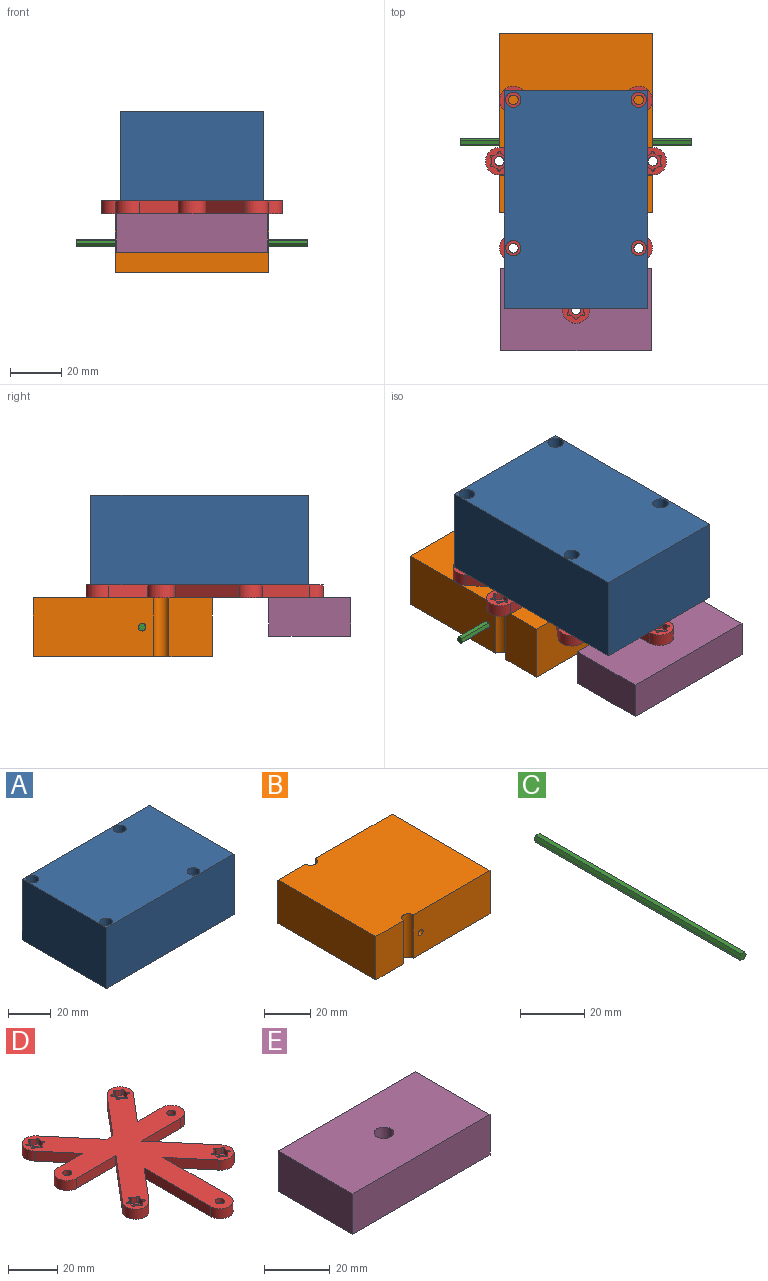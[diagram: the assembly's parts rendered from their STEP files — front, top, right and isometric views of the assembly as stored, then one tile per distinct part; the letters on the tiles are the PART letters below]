
ASSEMBLY  parts=5 mates=4
PART A: 10 faces, bbox 85x56x35 mm
  f0: plane 85x35mm, normal (0,1,0), area 2975mm2, adj f1,f3,f4,f5
  f1: plane 56x35mm, normal (-1,0,0), area 1960mm2, adj f0,f2,f4,f5
  f2: plane 85x35mm, normal (0,-1,0), area 2975mm2, adj f1,f3,f4,f5
  f3: plane 56x35mm, normal (1,0,0), area 1960mm2, adj f0,f2,f4,f5
  f4: plane 85x56mm, normal (0,0,1), area 4646.9mm2, adj f0,f1,f2,f3,f6,f7,f8,f9
  f5: plane 85x56mm, normal (0,0,-1), area 4646.9mm2, adj f0,f1,f2,f3,f6,f7,f8,f9
  f6: cylinder r=3mm len=35mm, axis (0,0,-1), area 659.7mm2, adj f4,f5
  f7: cylinder r=3mm len=35mm, axis (0,0,-1), area 659.7mm2, adj f4,f5
  f8: cylinder r=3mm len=35mm, axis (0,0,-1), area 659.7mm2, adj f4,f5
  f9: cylinder r=3mm len=35mm, axis (0,0,-1), area 659.7mm2, adj f4,f5
PART B: 11 faces, bbox 70x60x23 mm
  f0: plane 47x23mm, normal (0,1,0), area 1073.9mm2, adj f4,f6,f7,f9,f10
  f1: plane 23x17mm, normal (0,1,0), area 391mm2, adj f4,f5,f7,f9
  f2: plane 47x23mm, normal (0,-1,0), area 1073.9mm2, adj f4,f6,f7,f8,f10
  f3: plane 23x17mm, normal (0,-1,0), area 391mm2, adj f4,f5,f7,f8
  f4: plane 70x60mm, normal (0,0,1), area 4171.7mm2, adj f0,f1,f2,f3,f5,f6,f8,f9
  f5: plane 60x23mm, normal (-1,0,0), area 1380mm2, adj f1,f3,f4,f7
  f6: plane 60x23mm, normal (1,0,0), area 1380mm2, adj f0,f2,f4,f7
  f7: plane 70x60mm, normal (0,0,-1), area 4171.7mm2, adj f0,f1,f2,f3,f5,f6,f8,f9
  f8: cylinder r=3mm len=23mm, axis (0,0,-1), area 216.8mm2, adj f2,f3,f4,f7
  f9: cylinder r=3mm len=23mm, axis (0,0,-1), area 216.8mm2, adj f0,f1,f4,f7
  f10: cylinder r=1.5mm len=60mm, axis (0,1,0), area 565.5mm2, adj f0,f2
PART C: 8 faces, bbox 3x90x2.6 mm
  f0: plane 90x1.5mm, normal (0,0,-1), area 135mm2, adj f1,f5,f6,f7
  f1: plane 90x1.3mm, normal (0.87,0,-0.5), area 135mm2, adj f0,f2,f6,f7
  f2: plane 90x1.3mm, normal (0.87,0,0.5), area 135mm2, adj f1,f3,f6,f7
  f3: plane 90x1.5mm, normal (0,0,1), area 135mm2, adj f2,f4,f6,f7
  f4: plane 90x1.3mm, normal (-0.87,0,0.5), area 135mm2, adj f3,f5,f6,f7
  f5: plane 90x1.3mm, normal (-0.87,0,-0.5), area 135mm2, adj f0,f4,f6,f7
  f6: plane 3x2.6mm, normal (0,-1,0), area 5.8mm2, adj f0,f1,f2,f3,f4,f5
  f7: plane 3x2.6mm, normal (0,1,0), area 5.8mm2, adj f0,f1,f2,f3,f4,f5
PART D: 122 faces, bbox 70.8x92.8x5 mm
  f0: cylinder r=5.38mm len=10.75mm, axis (0,0,-1), area 84.4mm2, adj f1,f21,f22,f23
  f1: plane 22.65x5mm, normal (0,-1,0), area 113.2mm2, adj f0,f2,f22,f23
  f2: plane 25.16x21.25mm, normal (-0.76,0.65,0), area 164.7mm2, adj f1,f3,f22,f23
  f3: cylinder r=5.38mm len=9.48mm, axis (0,0,-1), area 84.4mm2, adj f2,f4,f22,f23
  f4: plane 17.78x15.02mm, normal (0.76,-0.65,0), area 116.4mm2, adj f3,f5,f22,f23
  f5: plane 38.31x5mm, normal (-1,0,0), area 191.5mm2, adj f4,f6,f22,f23
  f6: cylinder r=5.38mm len=10.75mm, axis (0,0,-1), area 84.4mm2, adj f5,f7,f22,f23
  f7: plane 38.31x5mm, normal (1,0,0), area 191.5mm2, adj f6,f8,f22,f23
  f8: plane 17.78x15.02mm, normal (-0.76,-0.65,0), area 116.4mm2, adj f7,f9,f22,f23
  f9: cylinder r=5.38mm len=9.48mm, axis (0,0,-1), area 84.4mm2, adj f8,f10,f22,f23
  f10: plane 25.16x21.25mm, normal (0.76,0.65,0), area 164.7mm2, adj f9,f11,f22,f23
  f11: plane 22.65x5mm, normal (0,-1,0), area 113.2mm2, adj f10,f12,f22,f23
  f12: cylinder r=5.38mm len=10.75mm, axis (0,0,-1), area 84.4mm2, adj f11,f13,f22,f23
  f13: plane 14.2x5mm, normal (0,1,0), area 71mm2, adj f12,f14,f22,f23
  f14: plane 15.16x12.8mm, normal (0.76,-0.65,0), area 99.2mm2, adj f13,f15,f22,f23
  f15: cylinder r=5.38mm len=9.48mm, axis (0,0,-1), area 84.4mm2, adj f14,f16,f22,f23
  f16: plane 22.09x18.67mm, normal (-0.76,0.65,0), area 144.6mm2, adj f15,f17,f22,f23
  f17: plane 5x3.46mm, normal (0,1,0), area 17.3mm2, adj f16,f18,f22,f23
  f18: plane 22.09x18.67mm, normal (0.76,0.65,0), area 144.6mm2, adj f17,f19,f22,f23
  f19: cylinder r=5.38mm len=9.48mm, axis (0,0,-1), area 84.4mm2, adj f18,f20,f22,f23
  f20: plane 15.16x12.8mm, normal (-0.76,-0.65,0), area 99.2mm2, adj f19,f21,f22,f23
  f21: plane 14.2x5mm, normal (0,1,0), area 71mm2, adj f0,f20,f22,f23
  f22: plane 92.75x70.75mm, normal (0,0,1), area 2521mm2, adj f0,f1,f2,f3,f4,f5,f6,f7
  f23: plane 92.75x70.75mm, normal (0,0,-1), area 2542.7mm2, adj f0,f1,f2,f3,f4,f5,f6,f7
  f24: plane 2.8x2.06mm, normal (-0.5,-0.87,0), area 6.6mm2, adj f23,f31,f35,f36
  f25: plane 2.8x2.38mm, normal (1,0,0), area 6.7mm2, adj f23,f30,f34,f36
  f26: plane 2.8x2.38mm, normal (-1,0,0), area 6.7mm2, adj f23,f32,f35,f36
  f27: plane 2.8x2.06mm, normal (0.5,0.87,0), area 6.6mm2, adj f23,f33,f34,f36
  f28: plane 2.8x2.06mm, normal (-0.5,0.87,0), area 6.6mm2, adj f23,f32,f33,f36
  f29: plane 2.8x2.06mm, normal (0.5,-0.87,0), area 6.6mm2, adj f23,f30,f31,f36
  f30: cylinder r=0.5mm len=2.8mm, axis (0,0,-1), area 5.9mm2, adj f23,f25,f29,f36
  f31: cylinder r=0.5mm len=2.8mm, axis (0,0,-1), area 5.9mm2, adj f23,f24,f29,f36
  f32: cylinder r=0.5mm len=2.8mm, axis (0,0,-1), area 5.9mm2, adj f23,f26,f28,f36
  f33: cylinder r=0.5mm len=2.8mm, axis (0,0,-1), area 5.9mm2, adj f23,f27,f28,f36
  f34: cylinder r=0.5mm len=2.8mm, axis (0,0,-1), area 5.9mm2, adj f23,f25,f27,f36
  f35: cylinder r=0.5mm len=2.8mm, axis (0,0,-1), area 5.9mm2, adj f23,f24,f26,f36
  f36: plane 7.75x6.85mm, normal (0,0,-1), area 21.7mm2, adj f24,f25,f26,f27,f28,f29,f30,f31
  f37: cylinder r=1.88mm len=3.75mm, axis (0,0,-1), area 25.9mm2, adj f22,f36
  f38: plane 2.8x2.06mm, normal (-0.5,-0.87,0), area 6.6mm2, adj f23,f45,f49,f50
  f39: plane 2.8x2.38mm, normal (1,0,0), area 6.7mm2, adj f23,f44,f48,f50
  f40: plane 2.8x2.38mm, normal (-1,0,0), area 6.7mm2, adj f23,f46,f49,f50
  f41: plane 2.8x2.06mm, normal (0.5,0.87,0), area 6.6mm2, adj f23,f47,f48,f50
  f42: plane 2.8x2.06mm, normal (-0.5,0.87,0), area 6.6mm2, adj f23,f46,f47,f50
  f43: plane 2.8x2.06mm, normal (0.5,-0.87,0), area 6.6mm2, adj f23,f44,f45,f50
  f44: cylinder r=0.5mm len=2.8mm, axis (0,0,-1), area 5.9mm2, adj f23,f39,f43,f50
  f45: cylinder r=0.5mm len=2.8mm, axis (0,0,-1), area 5.9mm2, adj f23,f38,f43,f50
  f46: cylinder r=0.5mm len=2.8mm, axis (0,0,-1), area 5.9mm2, adj f23,f40,f42,f50
  f47: cylinder r=0.5mm len=2.8mm, axis (0,0,-1), area 5.9mm2, adj f23,f41,f42,f50
  f48: cylinder r=0.5mm len=2.8mm, axis (0,0,-1), area 5.9mm2, adj f23,f39,f41,f50
  f49: cylinder r=0.5mm len=2.8mm, axis (0,0,-1), area 5.9mm2, adj f23,f38,f40,f50
  f50: plane 7.75x6.85mm, normal (0,0,-1), area 21.7mm2, adj f38,f39,f40,f41,f42,f43,f44,f45
  f51: cylinder r=1.88mm len=3.75mm, axis (0,0,-1), area 25.9mm2, adj f22,f50
  f52: cylinder r=1.88mm len=3.75mm, axis (0,0,1), area 25.9mm2, adj f23,f59
  f53: plane 2.8x2.06mm, normal (-0.5,-0.87,0), area 6.6mm2, adj f22,f59,f61,f65
  f54: plane 2.8x2.38mm, normal (1,0,0), area 6.7mm2, adj f22,f59,f60,f64
  f55: plane 2.8x2.38mm, normal (-1,0,0), area 6.7mm2, adj f22,f59,f62,f65
  f56: plane 2.8x2.06mm, normal (0.5,0.87,0), area 6.6mm2, adj f22,f59,f63,f64
  f57: plane 2.8x2.06mm, normal (-0.5,0.87,0), area 6.6mm2, adj f22,f59,f62,f63
  f58: plane 2.8x2.06mm, normal (0.5,-0.87,0), area 6.6mm2, adj f22,f59,f60,f61
  f59: plane 7.75x6.85mm, normal (0,0,1), area 21.7mm2, adj f52,f53,f54,f55,f56,f57,f58,f60
  f60: cylinder r=0.5mm len=2.8mm, axis (0,0,-1), area 5.9mm2, adj f22,f54,f58,f59
  f61: cylinder r=0.5mm len=2.8mm, axis (0,0,-1), area 5.9mm2, adj f22,f53,f58,f59
  f62: cylinder r=0.5mm len=2.8mm, axis (0,0,-1), area 5.9mm2, adj f22,f55,f57,f59
  f63: cylinder r=0.5mm len=2.8mm, axis (0,0,-1), area 5.9mm2, adj f22,f56,f57,f59
  f64: cylinder r=0.5mm len=2.8mm, axis (0,0,-1), area 5.9mm2, adj f22,f54,f56,f59
  f65: cylinder r=0.5mm len=2.8mm, axis (0,0,-1), area 5.9mm2, adj f22,f53,f55,f59
  f66: cylinder r=1.88mm len=3.75mm, axis (0,0,1), area 25.9mm2, adj f23,f73
  f67: plane 2.8x2.06mm, normal (-0.5,-0.87,0), area 6.6mm2, adj f22,f73,f75,f79
  f68: plane 2.8x2.38mm, normal (1,0,0), area 6.7mm2, adj f22,f73,f74,f78
  f69: plane 2.8x2.38mm, normal (-1,0,0), area 6.7mm2, adj f22,f73,f76,f79
  f70: plane 2.8x2.06mm, normal (0.5,0.87,0), area 6.6mm2, adj f22,f73,f77,f78
  f71: plane 2.8x2.06mm, normal (-0.5,0.87,0), area 6.6mm2, adj f22,f73,f76,f77
  f72: plane 2.8x2.06mm, normal (0.5,-0.87,0), area 6.6mm2, adj f22,f73,f74,f75
  f73: plane 7.75x6.85mm, normal (0,0,1), area 21.7mm2, adj f66,f67,f68,f69,f70,f71,f72,f74
  f74: cylinder r=0.5mm len=2.8mm, axis (0,0,-1), area 5.9mm2, adj f22,f68,f72,f73
  f75: cylinder r=0.5mm len=2.8mm, axis (0,0,-1), area 5.9mm2, adj f22,f67,f72,f73
  f76: cylinder r=0.5mm len=2.8mm, axis (0,0,-1), area 5.9mm2, adj f22,f69,f71,f73
  f77: cylinder r=0.5mm len=2.8mm, axis (0,0,-1), area 5.9mm2, adj f22,f70,f71,f73
  f78: cylinder r=0.5mm len=2.8mm, axis (0,0,-1), area 5.9mm2, adj f22,f68,f70,f73
  f79: cylinder r=0.5mm len=2.8mm, axis (0,0,-1), area 5.9mm2, adj f22,f67,f69,f73
  f80: cylinder r=1.88mm len=3.75mm, axis (0,0,1), area 25.9mm2, adj f23,f87
  f81: plane 2.8x2.06mm, normal (-0.5,-0.87,0), area 6.6mm2, adj f22,f87,f89,f93
  f82: plane 2.8x2.38mm, normal (1,0,0), area 6.7mm2, adj f22,f87,f88,f92
  f83: plane 2.8x2.38mm, normal (-1,0,0), area 6.7mm2, adj f22,f87,f90,f93
  f84: plane 2.8x2.06mm, normal (0.5,0.87,0), area 6.6mm2, adj f22,f87,f91,f92
  f85: plane 2.8x2.06mm, normal (-0.5,0.87,0), area 6.6mm2, adj f22,f87,f90,f91
  f86: plane 2.8x2.06mm, normal (0.5,-0.87,0), area 6.6mm2, adj f22,f87,f88,f89
  f87: plane 7.75x6.85mm, normal (0,0,1), area 21.7mm2, adj f80,f81,f82,f83,f84,f85,f86,f88
  f88: cylinder r=0.5mm len=2.8mm, axis (0,0,-1), area 5.9mm2, adj f22,f82,f86,f87
  f89: cylinder r=0.5mm len=2.8mm, axis (0,0,-1), area 5.9mm2, adj f22,f81,f86,f87
  f90: cylinder r=0.5mm len=2.8mm, axis (0,0,-1), area 5.9mm2, adj f22,f83,f85,f87
  f91: cylinder r=0.5mm len=2.8mm, axis (0,0,-1), area 5.9mm2, adj f22,f84,f85,f87
  f92: cylinder r=0.5mm len=2.8mm, axis (0,0,-1), area 5.9mm2, adj f22,f82,f84,f87
  f93: cylinder r=0.5mm len=2.8mm, axis (0,0,-1), area 5.9mm2, adj f22,f81,f83,f87
  f94: cylinder r=1.88mm len=3.75mm, axis (0,0,1), area 25.9mm2, adj f23,f101
  f95: plane 2.8x2.06mm, normal (-0.5,-0.87,0), area 6.6mm2, adj f22,f101,f103,f107
  f96: plane 2.8x2.38mm, normal (1,0,0), area 6.7mm2, adj f22,f101,f102,f106
  f97: plane 2.8x2.38mm, normal (-1,0,0), area 6.7mm2, adj f22,f101,f104,f107
  f98: plane 2.8x2.06mm, normal (0.5,0.87,0), area 6.6mm2, adj f22,f101,f105,f106
  f99: plane 2.8x2.06mm, normal (-0.5,0.87,0), area 6.6mm2, adj f22,f101,f104,f105
  f100: plane 2.8x2.06mm, normal (0.5,-0.87,0), area 6.6mm2, adj f22,f101,f102,f103
  f101: plane 7.75x6.85mm, normal (0,0,1), area 21.7mm2, adj f94,f95,f96,f97,f98,f99,f100,f102
  f102: cylinder r=0.5mm len=2.8mm, axis (0,0,-1), area 5.9mm2, adj f22,f96,f100,f101
  f103: cylinder r=0.5mm len=2.8mm, axis (0,0,-1), area 5.9mm2, adj f22,f95,f100,f101
  f104: cylinder r=0.5mm len=2.8mm, axis (0,0,-1), area 5.9mm2, adj f22,f97,f99,f101
  f105: cylinder r=0.5mm len=2.8mm, axis (0,0,-1), area 5.9mm2, adj f22,f98,f99,f101
  f106: cylinder r=0.5mm len=2.8mm, axis (0,0,-1), area 5.9mm2, adj f22,f96,f98,f101
  f107: cylinder r=0.5mm len=2.8mm, axis (0,0,-1), area 5.9mm2, adj f22,f95,f97,f101
  f108: plane 2.8x2.06mm, normal (-0.5,-0.87,0), area 6.6mm2, adj f23,f115,f119,f120
  f109: plane 2.8x2.38mm, normal (1,0,0), area 6.6mm2, adj f23,f114,f118,f120
  f110: plane 2.8x2.38mm, normal (-1,0,0), area 6.6mm2, adj f23,f116,f119,f120
  f111: plane 2.8x2.06mm, normal (0.5,0.87,0), area 6.6mm2, adj f23,f117,f118,f120
  f112: plane 2.8x2.06mm, normal (-0.5,0.87,0), area 6.6mm2, adj f23,f116,f117,f120
  f113: plane 2.8x2.06mm, normal (0.5,-0.87,0), area 6.6mm2, adj f23,f114,f115,f120
  f114: cylinder r=0.5mm len=2.8mm, axis (0,0,-1), area 5.9mm2, adj f23,f109,f113,f120
  f115: cylinder r=0.5mm len=2.8mm, axis (0,0,-1), area 5.9mm2, adj f23,f108,f113,f120
  f116: cylinder r=0.5mm len=2.8mm, axis (0,0,-1), area 5.9mm2, adj f23,f110,f112,f120
  f117: cylinder r=0.5mm len=2.8mm, axis (0,0,-1), area 5.9mm2, adj f23,f111,f112,f120
  f118: cylinder r=0.5mm len=2.8mm, axis (0,0,-1), area 5.9mm2, adj f23,f109,f111,f120
  f119: cylinder r=0.5mm len=2.8mm, axis (0,0,-1), area 5.9mm2, adj f23,f108,f110,f120
  f120: plane 7.75x6.85mm, normal (0,0,-1), area 21.7mm2, adj f108,f109,f110,f111,f112,f113,f114,f115
  f121: cylinder r=1.88mm len=3.75mm, axis (0,0,-1), area 25.9mm2, adj f22,f120
PART E: 7 faces, bbox 59x32x15 mm
  f0: plane 59x15mm, normal (0,1,0), area 885mm2, adj f1,f3,f4,f5
  f1: plane 32x15mm, normal (-1,0,0), area 480mm2, adj f0,f2,f4,f5
  f2: plane 59x15mm, normal (0,-1,0), area 885mm2, adj f1,f3,f4,f5
  f3: plane 32x15mm, normal (1,0,0), area 480mm2, adj f0,f2,f4,f5
  f4: plane 59x32mm, normal (0,0,1), area 1859.7mm2, adj f0,f1,f2,f3,f6
  f5: plane 59x32mm, normal (0,0,-1), area 1859.7mm2, adj f0,f1,f2,f3,f6
  f6: cylinder r=3mm len=15mm, axis (0,0,-1), area 282.7mm2, adj f4,f5
PLACE A rot(axis=(0,0,-1),90deg) t=(-18.93,36.11,2.34)mm
PLACE B rot(axis=(0.71,0.71,0),180deg) t=(-19.82,66.62,-2.66)mm
PLACE C rot(axis=(-0.4,0.4,0.83),100.9deg) t=(18.1,38.46,-60.9)mm
PLACE D rot(axis=(0,1,0),180deg) t=(-0.86,-6.39,2.34)mm fixed
PLACE E rot(axis=(0,1,0),180deg) t=(-3.97,-19.89,-2.66)mm
MATE fastened A.f8 <-> D.f9  axis (0,0,-1) through (-25.36,-25.39,2.34)mm
MATE fastened D.f12 <-> B.f8  axis (0,0,1) through (-30.86,8.61,-2.66)mm
MATE revolute C.f6 <-> B.f10  axis (1,0,0) through (44.14,16.11,-14.16)mm
MATE fastened E.f6 <-> D.f6  axis (0,0,1) through (-0.86,-49.39,-2.66)mm
